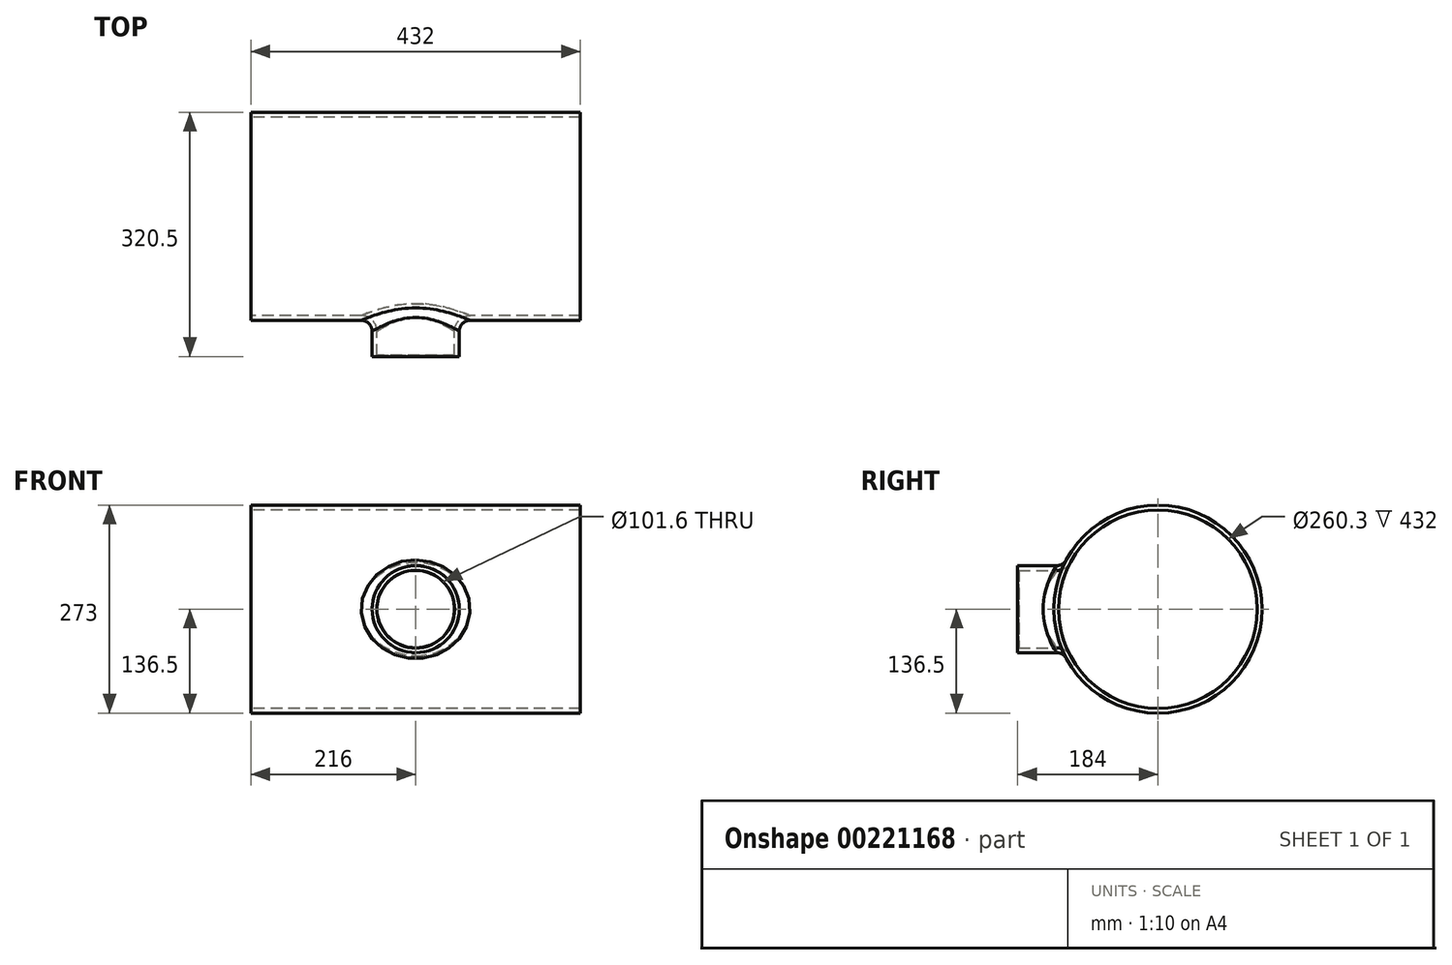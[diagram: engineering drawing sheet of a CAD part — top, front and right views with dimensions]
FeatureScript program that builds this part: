
annotation { "Feature Type Name" : "Feature", "Feature Type Description" : "" }
export const myFeature = defineFeature(function(context is Context, id is Id, definition is map)
    precondition{}
    {
        {
            assignVariable(context, id + "F0", {"name" : "T", "anyValue" : 6.35});
        }
        {
            assignVariable(context, id + "F1", {"name" : "d", "anyValue" : 114.3});
        }
        {
            assignVariable(context, id + "F2", {"name" : "A", "anyValue" : 216});
        }
        {
            assignVariable(context, id + "F3", {"name" : "B", "anyValue" : 184});
        }
        {
            var Q0;
            Q0=qCreatedBy(makeId("Right.planeOp"),FACE);
            var sketch = newSketch(context, id + "F4", { "sketchPlane" : qUnion([Q0])});
            skCircle(sketch, "E0", {"center": v(0, 0) * mm, "radius": 136.5 * mm});
            skSolve(sketch);
        }
        {
            var Q0;
            Q0=qCreatedBy(makeId("Front.planeOp"),FACE);
            var sketch = newSketch(context, id + "F5", { "sketchPlane" : qUnion([Q0])});
            skCircle(sketch, "E1", {"center": v(0, 0) * mm, "radius": 57.15 * mm});
            skSolve(sketch);
        }
        {
            var Q0;
            Q0=makeQuery(id+"F4.imprint","IMPRINT",FACE,{"disambiguationData":[TD([[makeQuery(id+"F4.imprint","IMPRINT",EDGE,{"derivedFrom":sQuery(id+"F4.wireOp",EDGE,"E0")}),1.0]])]});
            extrude(context, id + "F6", {"entities" : qUnion([Q0]), "endBound" : BoundingType.SYMMETRIC, "depth" : (2 * getVariable(context, 'A')) * mm});
        }
        {
            var Q0;
            Q0=makeQuery(id+"F5.imprint","IMPRINT",FACE,{"disambiguationData":[TD([[makeQuery(id+"F5.imprint","IMPRINT",EDGE,{"derivedFrom":sQuery(id+"F5.wireOp",EDGE,"E1")}),1.0]])]});
            extrude(context, id + "F7", {"entities" : qUnion([Q0]), "operationType" : NewBodyOperationType.ADD, "depth" : (getVariable(context, 'B')) * mm});
        }
        {
            var Q0;
            Q0=makeQuery(id+"F7.boolean.opBoolean","INTERSECT",EDGE,{"derivedFrom":[makeQuery(id+"F6.opExtrude","SWEPT_FACE",FACE,{"disambiguationData":[OSD([sQuery(id+"F4.wireOp",EDGE,"E0")])]}),makeQuery(id+"F7.opExtrude","SWEPT_FACE",FACE,{"disambiguationData":[OSD([sQuery(id+"F5.wireOp",EDGE,"E1")])]})]});
            fillet(context, id + "F8", {"entities" : qUnion([Q0]), "radius" : (getVariable(context, 'd') / 8) * mm, "tangentPropagation" : true, "allowEdgeOverflow" : false});
        }
        {
            var Q0;
            Q0=makeQuery(id+"F6.opExtrude","CAP_FACE",FACE,{"disambiguationData":[OSD([sQuery(id+"F4.wireOp",EDGE,"E0")])],"isStart":false});
            var Q1;
            Q1=makeQuery(id+"F6.opExtrude","CAP_FACE",FACE,{"disambiguationData":[OSD([sQuery(id+"F4.wireOp",EDGE,"E0")])],"isStart":true});
            var Q2;
            Q2=makeQuery(id+"F7.opExtrude","CAP_FACE",FACE,{"disambiguationData":[OSD([sQuery(id+"F5.wireOp",EDGE,"E1")])],"isStart":false});
            shell(context, id + "F9", {"entities" : qUnion([Q0, Q1, Q2]), "thickness" : (getVariable(context, 'T')) * mm});
        }
        {
            var Q0;
            Q0=qCreatedBy(makeId("Right.planeOp"),FACE);
            var sketch = newSketch(context, id + "F10", { "sketchPlane" : qUnion([Q0])});
            skLineSegment(sketch, "E2", {"start": v(-184, 51.05) * mm, "end": v(-146, 44.95) * mm});
            skLineSegment(sketch, "E3", {"start": v(-146, 44.95) * mm, "end": v(-184, 44.95) * mm});
            skLineSegment(sketch, "E4", {"start": v(-184, 44.95) * mm, "end": v(-184, 51.05) * mm});
            skLineSegment(sketch, "E5", {"start": v(0, 0) * mm, "end": v(-278.55, 0) * mm, "construction": true});
            skSolve(sketch);
        }
        {
            var Q0;
            Q0=makeQuery(id+"F10.imprint","IMPRINT",FACE,{"disambiguationData":[TD([[makeQuery(id+"F10.imprint","IMPRINT",EDGE,{"derivedFrom":sQuery(id+"F10.wireOp",EDGE,"E2")}),-1.0]])]});
            var Q1;
            Q1=sQuery(id+"F10.wireOp",EDGE,"E5");
            revolve(context, id + "F11", {"operationType" : NewBodyOperationType.REMOVE, "entities" : qUnion([Q0]), "axis" : qUnion([Q1]), "revolveType" : RevolveType.FULL, "oppositeDirection" : true});
        }
    });
